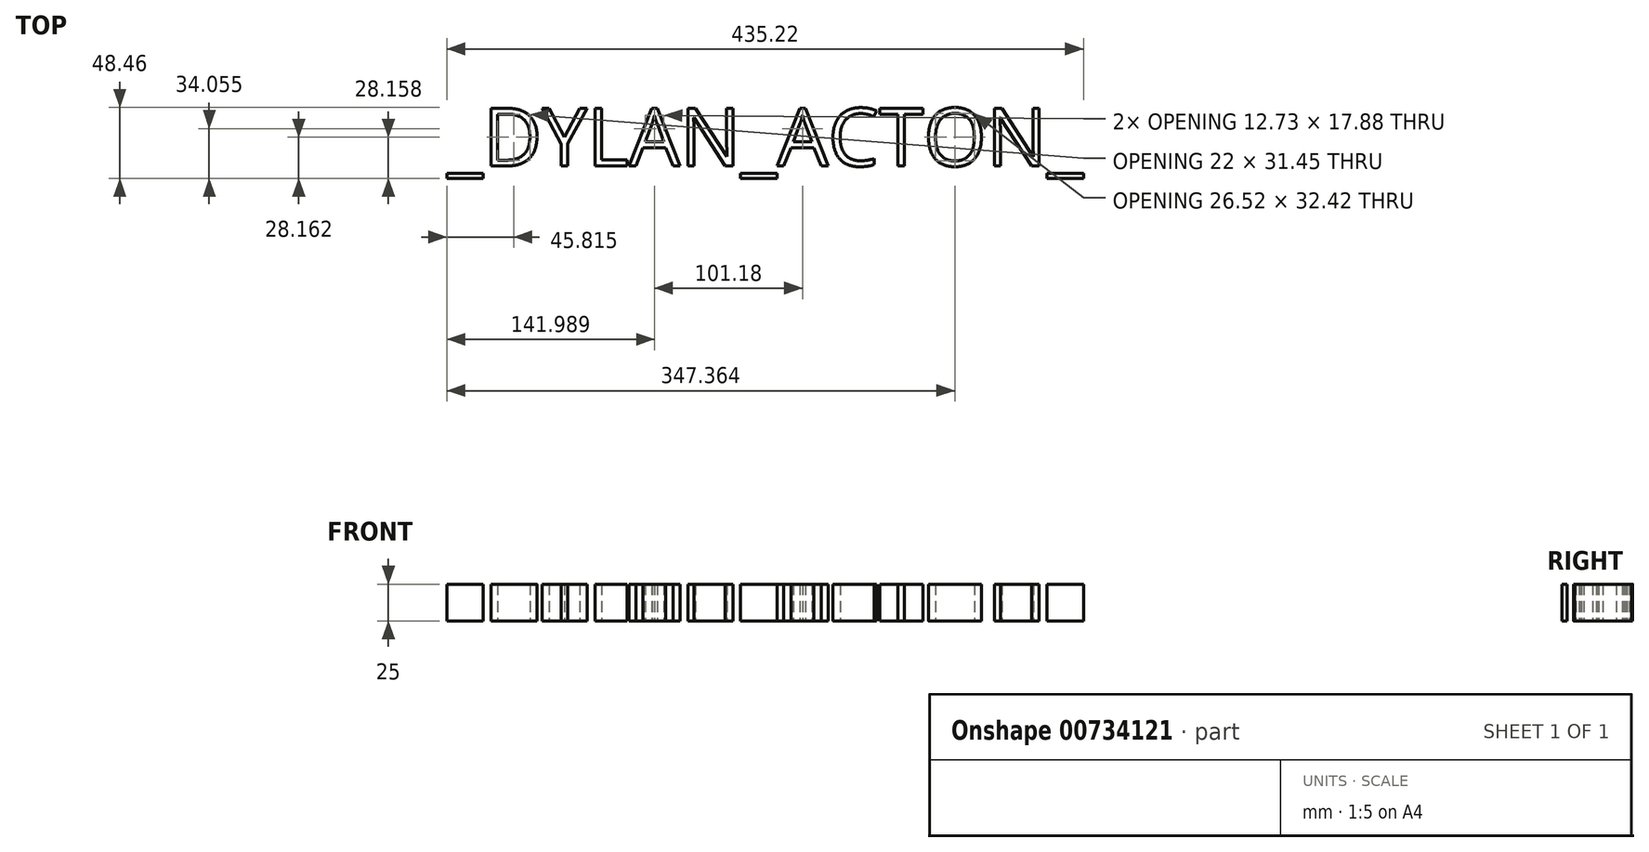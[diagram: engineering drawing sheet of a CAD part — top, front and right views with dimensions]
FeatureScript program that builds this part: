
annotation { "Feature Type Name" : "Feature", "Feature Type Description" : "" }
export const myFeature = defineFeature(function(context is Context, id is Id, definition is map)
    precondition{}
    {
        {
            var Q0;
            Q0=qCreatedBy(makeId("Top.planeOp"),FACE);
            var sketch = newSketch(context, id + "F0", { "sketchPlane" : qUnion([Q0])});
            skText(sketch, "E0", { "text": "_DYLAN_ACTON_", "fontName": "OpenSans-Regular.ttf"});
            const initialGuessF0  = {"E0": [-0.18182, 0.00324, 1, 0, 0.0397]};
            skSetInitialGuess(sketch, initialGuessF0);
            skSolve(sketch);
        }
        {
            var Q0;
            Q0 = qSketchRegion(id + "F0", true);
            extrude(context, id + "F1", {"entities" : qUnion([Q0]), "depth" : 25 * mm, "offsetDistance" : 25 * mm});
        }
    });
